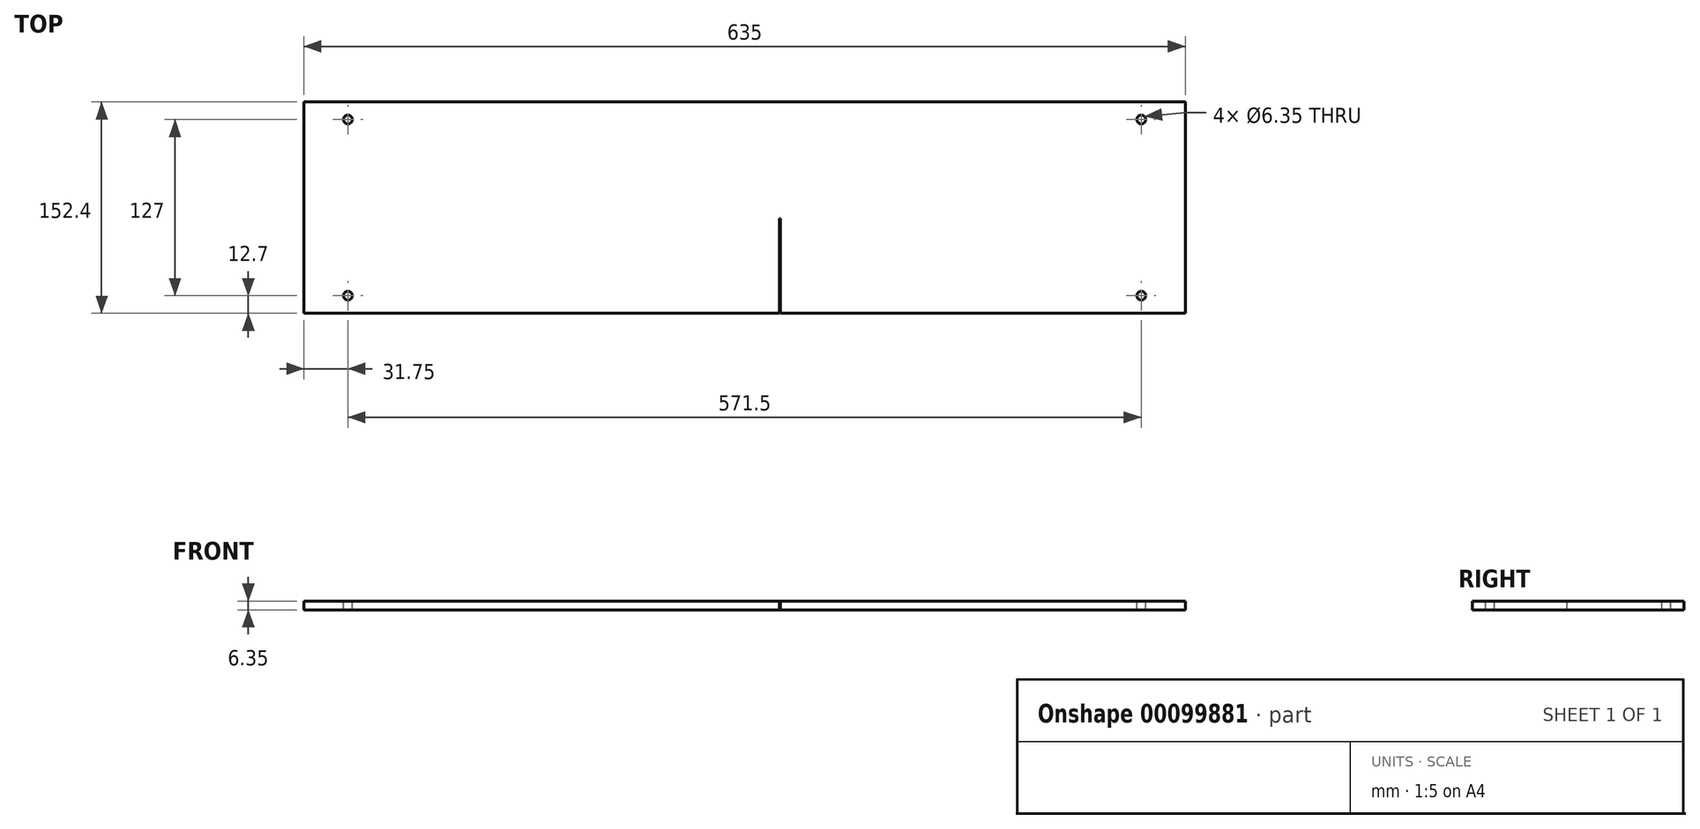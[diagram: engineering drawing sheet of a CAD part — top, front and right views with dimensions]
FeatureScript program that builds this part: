
annotation { "Feature Type Name" : "Feature", "Feature Type Description" : "" }
export const myFeature = defineFeature(function(context is Context, id is Id, definition is map)
    precondition{}
    {
        {
            var Q0;
            Q0=qCreatedBy(makeId("Top.planeOp"),FACE);
            var sketch = newSketch(context, id + "F0", { "sketchPlane" : qUnion([Q0])});
            skLineSegment(sketch, "E0.bottom", {"start": v(317.5, -76.2) * mm, "end": v(-317.5, -76.2) * mm});
            skLineSegment(sketch, "E0.top", {"start": v(317.5, 76.2) * mm, "end": v(-317.5, 76.2) * mm});
            skLineSegment(sketch, "E0.left", {"start": v(317.5, -76.2) * mm, "end": v(317.5, 76.2) * mm});
            skLineSegment(sketch, "E0.right", {"start": v(-317.5, -76.2) * mm, "end": v(-317.5, 76.2) * mm});
            skPoint(sketch, "E0.middle", {"position": v(0, 0) * mm});
            skSolve(sketch);
        }
        {
            var Q0;
            Q0=makeQuery(id+"F0.imprint","IMPRINT",FACE,{"disambiguationData":[TD([[makeQuery(id+"F0.imprint","IMPRINT",EDGE,{"derivedFrom":sQuery(id+"F0.wireOp",EDGE,"E0.bottom")}),-1.0]])]});
            extrude(context, id + "F1", {"entities" : qUnion([Q0]), "depth" : 6.35 * mm});
        }
        {
            var Q0;
            Q0=makeQuery(id+"F1.opExtrude","CAP_FACE",FACE,{"disambiguationData":[OSD([sQuery(id+"F0.wireOp",EDGE,"E0.bottom"),sQuery(id+"F0.wireOp",EDGE,"E0.top"),sQuery(id+"F0.wireOp",EDGE,"E0.left"),sQuery(id+"F0.wireOp",EDGE,"E0.right")])],"isStart":false});
            var sketch = newSketch(context, id + "F2", { "sketchPlane" : qUnion([Q0])});
            skPoint(sketch, "E1", {"position": v(-285.75, -63.5) * mm});
            skPoint(sketch, "E2.MirrorP", {"position": v(-285.75, 63.5) * mm});
            skPoint(sketch, "E3.MirrorP", {"position": v(285.75, -63.5) * mm});
            skPoint(sketch, "E4.MirrorP", {"position": v(285.75, 63.5) * mm});
            skSolve(sketch);
        }
        {
            var Q0;
            Q0=sQuery(id+"F2.wireOp",VERTEX,"E2.MirrorP");
            var Q1;
            Q1=sQuery(id+"F2.wireOp",VERTEX,"E1");
            var Q2;
            Q2=sQuery(id+"F2.wireOp",VERTEX,"E3.MirrorP");
            var Q3;
            Q3=sQuery(id+"F2.wireOp",VERTEX,"E4.MirrorP");
            var Q4;
            Q4=makeQuery(id+"F1.opExtrude","SWEPT_BODY",BODY,{"disambiguationData":[OSD([sQuery(id+"F0.wireOp",EDGE,"E0.bottom"),sQuery(id+"F0.wireOp",EDGE,"E0.top"),sQuery(id+"F0.wireOp",EDGE,"E0.left"),sQuery(id+"F0.wireOp",EDGE,"E0.right")])]});
            hole(context, id + "F3", {"style" : HoleStyle.SIMPLE, "endStyle" : HoleEndStyle.THROUGH, "holeDiameter" : 6.35 * mm, "locations" : qUnion([Q0, Q1, Q2, Q3]), "scope" : qUnion([Q4]), "isTappedThrough" : true});
        }
        {
            var Q0;
            Q0=makeQuery(id+"F1.opExtrude","CAP_FACE",FACE,{"disambiguationData":[OSD([sQuery(id+"F0.wireOp",EDGE,"E0.bottom"),sQuery(id+"F0.wireOp",EDGE,"E0.top"),sQuery(id+"F0.wireOp",EDGE,"E0.left"),sQuery(id+"F0.wireOp",EDGE,"E0.right")])],"isStart":false});
            var sketch = newSketch(context, id + "F4", { "sketchPlane" : qUnion([Q0])});
            skLineSegment(sketch, "E5.bottom", {"start": v(25.7, -76.2) * mm, "end": v(25.1, -76.2) * mm});
            skLineSegment(sketch, "E5.top", {"start": v(25.7, -7.94) * mm, "end": v(25.1, -7.94) * mm});
            skLineSegment(sketch, "E5.left", {"start": v(25.7, -76.2) * mm, "end": v(25.7, -7.94) * mm});
            skLineSegment(sketch, "E5.right", {"start": v(25.1, -76.2) * mm, "end": v(25.1, -7.94) * mm});
            skPoint(sketch, "E5.middle", {"position": v(25.4, -42.07) * mm});
            skSolve(sketch);
        }
        {
            var Q0;
            Q0 = qSketchRegion(id + "F4", true);
            extrude(context, id + "F5", {"entities" : qUnion([Q0]), "operationType" : NewBodyOperationType.REMOVE, "oppositeDirection" : true, "depth" : 25.4 * mm});
        }
    });
